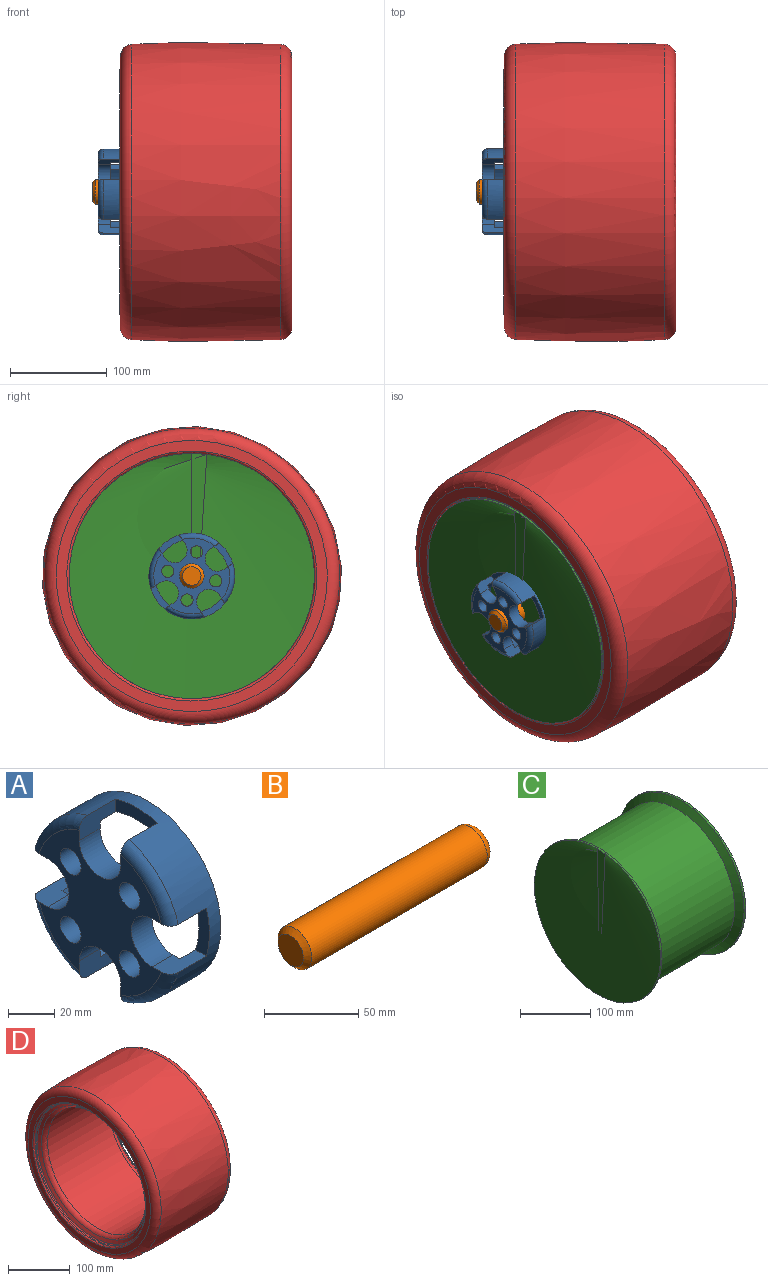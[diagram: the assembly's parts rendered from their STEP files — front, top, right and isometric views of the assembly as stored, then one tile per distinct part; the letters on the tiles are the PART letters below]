
ASSEMBLY  parts=4 mates=3
PART A: 29 faces, bbox 29.2x92.2x92.2 mm
  f0: cylinder r=38.1mm len=76.2mm, axis (1,0,0), area 2965.7mm2, adj f2,f8,f10,f11,f12,f14,f15,f16
  f1: plane 74.53x74.53mm, normal (-1,0,0), area 2645.6mm2, adj f3,f4,f5,f6,f9,f10,f11,f13
  f2: plane 71.84x71.84mm, normal (1,0,0), area 2468mm2, adj f0,f9,f10,f11,f13,f14,f15,f17
  f3: torus R=39.37mm, axis (-1,0,0), area 328.2mm2, adj f1,f7,f19,f23
  f4: torus R=39.37mm, axis (-1,0,0), area 328.2mm2, adj f1,f7,f14,f18
  f5: torus R=39.37mm, axis (-1,0,0), area 328.2mm2, adj f1,f7,f11,f15
  f6: torus R=39.37mm, axis (-1,0,0), area 328.2mm2, adj f1,f7,f10,f22
  f7: cylinder r=44.45mm len=88.9mm, axis (1,0,0), area 4972.7mm2, adj f3,f4,f5,f6,f8,f10,f11,f12
  f8: plane 88.9x88.9mm, normal (1,0,0), area 1646.8mm2, adj f0,f7
  f9: cylinder r=12.7mm len=25.4mm, axis (-1,0,0), area 506.7mm2, adj f1,f2,f10,f11
  f10: plane 22.23x10.85mm, normal (0,0,-1), area 195.6mm2, adj f0,f1,f2,f6,f7,f9,f12
  f11: plane 22.23x10.85mm, normal (0,0,1), area 195.6mm2, adj f0,f1,f2,f5,f7,f9,f12
  f12: plane 25.4x8.53mm, normal (-1,0,0), area 164mm2, adj f0,f7,f10,f11
  f13: cylinder r=12.7mm len=25.4mm, axis (-1,0,0), area 506.7mm2, adj f1,f2,f14,f15
  f14: plane 22.23x10.85mm, normal (0,1,0), area 195.6mm2, adj f0,f1,f2,f4,f7,f13,f16
  f15: plane 22.23x10.85mm, normal (0,-1,0), area 195.6mm2, adj f0,f1,f2,f5,f7,f13,f16
  f16: plane 25.4x8.53mm, normal (-1,0,0), area 164mm2, adj f0,f7,f14,f15
  f17: cylinder r=12.7mm len=25.4mm, axis (-1,0,0), area 506.7mm2, adj f1,f2,f18,f19
  f18: plane 22.23x10.85mm, normal (0,0,1), area 195.6mm2, adj f0,f1,f2,f4,f7,f17,f20
  f19: plane 22.23x10.85mm, normal (0,0,-1), area 195.6mm2, adj f0,f1,f2,f3,f7,f17,f20
  f20: plane 25.4x8.53mm, normal (-1,0,0), area 164mm2, adj f0,f7,f18,f19
  f21: cylinder r=12.7mm len=25.4mm, axis (-1,0,0), area 506.7mm2, adj f1,f2,f22,f23
  f22: plane 22.23x10.85mm, normal (0,-1,0), area 195.6mm2, adj f0,f1,f2,f6,f7,f21,f24
  f23: plane 22.23x10.85mm, normal (0,1,0), area 195.6mm2, adj f0,f1,f2,f3,f7,f21,f24
  f24: plane 25.4x8.53mm, normal (-1,0,0), area 164mm2, adj f0,f7,f22,f23
  f25: cylinder r=6.35mm len=12.7mm, axis (-1,0,0), area 506.7mm2, adj f1,f2
  f26: cylinder r=6.35mm len=12.7mm, axis (-1,0,0), area 506.7mm2, adj f1,f2
  f27: cylinder r=6.35mm len=12.7mm, axis (-1,0,0), area 506.7mm2, adj f1,f2
  f28: cylinder r=6.35mm len=12.7mm, axis (-1,0,0), area 506.7mm2, adj f1,f2
PART B: 5 faces, bbox 139.7x27.5x27.5 mm
  f0: cylinder r=12.7mm len=131.45mm, axis (1,0,0), area 10488.8mm2, adj f3,f4
  f1: plane 19.05x19.05mm, normal (-1,0,0), area 285mm2, adj f4
  f2: plane 15.24x15.24mm, normal (1,0,0), area 182.4mm2, adj f3
  f3: torus R=7.62mm, axis (1,0,0), area 544.2mm2, adj f0,f2
  f4: cone r=12.7mm half-angle=45deg, axis (1,0,0), area 313.5mm2, adj f0,f1
PART C: 238 faces, bbox 171.5x281.6x281.6 mm
  f0: cone r=44.45mm half-angle=87.1deg, axis (1,0,0), area 887.3mm2, adj f35,f36,f66,f72,f80,f83,f98,f101
  f1: cone r=44.45mm half-angle=87.1deg, axis (1,0,0), area 649.3mm2, adj f35,f36,f73,f81,f99,f145,f146
  f2: cone r=44.45mm half-angle=87.1deg, axis (1,0,0), area 887.3mm2, adj f35,f36,f62,f65,f82,f85,f100,f103
  f3: cone r=44.45mm half-angle=87.1deg, axis (1,0,0), area 887.3mm2, adj f35,f36,f43,f61,f84,f87,f102,f105
  f4: cone r=44.45mm half-angle=87.1deg, axis (1,0,0), area 887.3mm2, adj f35,f36,f54,f57,f76,f79,f92,f95
  f5: cone r=44.45mm half-angle=87.1deg, axis (1,0,0), area 649.3mm2, adj f35,f36,f53,f78,f94,f162,f165
  f6: cone r=44.45mm half-angle=87.1deg, axis (1,0,0), area 649.3mm2, adj f35,f36,f49,f74,f88,f183,f186
  f7: cone r=44.45mm half-angle=87.1deg, axis (1,0,0), area 649.3mm2, adj f35,f36,f58,f77,f93,f166,f168
  f8: cone r=44.45mm half-angle=87.1deg, axis (-1,0,0), area 442.3mm2, adj f38,f39,f127,f129,f130,f131
  f9: cone r=44.45mm half-angle=87.1deg, axis (-1,0,0), area 442.3mm2, adj f38,f39,f139,f141,f142,f143
  f10: cone r=44.45mm half-angle=87.1deg, axis (-1,0,0), area 442.3mm2, adj f38,f39,f115,f117,f118,f119
  f11: cone r=44.45mm half-angle=87.1deg, axis (-1,0,0), area 442.3mm2, adj f38,f39,f106,f107,f206,f208
  f12: cone r=44.45mm half-angle=87.1deg, axis (-1,0,0), area 442.3mm2, adj f38,f39,f214,f216,f231,f233
  f13: cone r=44.45mm half-angle=87.1deg, axis (-1,0,0), area 442.3mm2, adj f38,f39,f159,f163,f224,f225
  f14: cone r=44.45mm half-angle=87.1deg, axis (-1,0,0), area 442.3mm2, adj f38,f39,f187,f189,f190,f191
  f15: cone r=44.45mm half-angle=87.1deg, axis (-1,0,0), area 442.3mm2, adj f38,f39,f169,f172,f232,f234
  f16: cone r=107.95mm half-angle=71.6deg, axis (-1,0,0), area 10024.8mm2, adj f32,f33
  f17: cylinder r=107.95mm len=215.9mm, axis (-1,0,0), area 5780mm2, adj f33,f35
  f18: cone r=44.45mm half-angle=87.1deg, axis (1,0,0), area 887.3mm2, adj f35,f36,f42,f50,f75,f86,f89,f104
  f19: cylinder r=44.45mm len=88.9mm, axis (-1,0,0), area 2789.9mm2, adj f20,f36
  f20: plane 88.9x88.9mm, normal (-1,0,0), area 1646.8mm2, adj f19,f21
  f21: cylinder r=38.1mm len=82.55mm, axis (-1,0,0), area 19761.6mm2, adj f20,f22
  f22: plane 76.2x76.2mm, normal (-1,0,0), area 4560.4mm2, adj f21
  f23: plane 69.85x69.85mm, normal (1,0,0), area 3832mm2, adj f37
  f24: cylinder r=44.45mm len=88.9mm, axis (-1,0,0), area 10770.5mm2, adj f37,f38
  f25: cone r=44.45mm half-angle=87.1deg, axis (-1,0,0), area 442.3mm2, adj f38,f39,f199,f201,f205,f207
  f26: cylinder r=107.95mm len=215.9mm, axis (-1,0,0), area 74692.2mm2, adj f34,f39
  f27: cone r=107.95mm half-angle=71.6deg, axis (1,0,0), area 10024.8mm2, adj f28,f34
  f28: cylinder r=127mm len=254mm, axis (-1,0,0), area 2533.5mm2, adj f27,f29
  f29: cone r=114.3mm half-angle=63.4deg, axis (1,0,0), area 10763.8mm2, adj f28,f30
  f30: cylinder r=114.3mm len=228.6mm, axis (-1,0,0), area 109448.8mm2, adj f29,f31
  f31: cone r=114.3mm half-angle=63.4deg, axis (-1,0,0), area 10763.8mm2, adj f30,f32
  f32: cylinder r=127mm len=254mm, axis (-1,0,0), area 2533.5mm2, adj f16,f31
  f33: torus R=117.47mm, axis (1,0,0), area 8240.7mm2, adj f16,f17
  f34: torus R=117.47mm, axis (1,0,0), area 8240.7mm2, adj f26,f27
  f35: torus R=98.42mm, axis (-1,0,0), area 9680.5mm2, adj f0,f1,f2,f3,f4,f5,f6,f7
  f36: torus R=53.98mm, axis (-1,0,0), area 3935.7mm2, adj f0,f1,f2,f3,f4,f5,f6,f7
  f37: torus R=34.92mm, axis (-1,0,0), area 3853.3mm2, adj f23,f24
  f38: torus R=53.98mm, axis (-1,0,0), area 3464.9mm2, adj f8,f9,f10,f11,f12,f13,f14,f15
  f39: torus R=98.42mm, axis (-1,0,0), area 8487.7mm2, adj f8,f9,f10,f11,f12,f13,f14,f15
  f40: cylinder r=50.8mm len=9.79mm, axis (1,0,0), area 46.1mm2, adj f36,f104,f105,f213
  f41: cylinder r=98.42mm len=28.43mm, axis (1,0,0), area 93.3mm2, adj f35,f86,f87,f202
  f42: plane 32.91x6.73mm, normal (0,0.98,0.19), area 170.7mm2, adj f18,f86,f104,f207,f209
  f43: plane 25.3x22mm, normal (0,-0.75,0.66), area 170.7mm2, adj f3,f87,f105,f208,f210
  f44: cylinder r=50.8mm len=6.72mm, axis (1,0,0), area 31.7mm2, adj f90,f91,f174,f181
  f45: plane 17.38x1.73mm, normal (0,-0.02,1), area 14.8mm2, adj f90,f166,f167,f169,f173
  f46: plane 13.51x10.94mm, normal (0,-0.78,-0.63), area 14.8mm2, adj f91,f182,f186,f188,f189
  f47: cylinder r=50.8mm len=9.79mm, axis (1,0,0), area 46.1mm2, adj f36,f88,f89,f196
  f48: cylinder r=98.42mm len=26.67mm, axis (1,0,0), area 93.3mm2, adj f35,f74,f75,f195
  f49: plane 26.05x21.1mm, normal (0,0.63,0.78), area 170.7mm2, adj f6,f74,f88,f190,f192
  f50: plane 33.52x6.73mm, normal (0,-1,0.02), area 170.7mm2, adj f18,f75,f89,f200,f201
  f51: cylinder r=50.8mm len=9.79mm, axis (1,0,0), area 46.1mm2, adj f36,f94,f95,f219
  f52: cylinder r=98.42mm len=24.11mm, axis (1,0,0), area 93.3mm2, adj f35,f78,f79,f220
  f53: plane 33.11x6.73mm, normal (0,-0.99,0.16), area 170.7mm2, adj f5,f78,f94,f223,f225
  f54: plane 29.32x16.25mm, normal (0,0.48,-0.87), area 170.7mm2, adj f4,f79,f95,f214,f215
  f55: cylinder r=50.8mm len=9.79mm, axis (1,0,0), area 46.1mm2, adj f36,f92,f93,f226
  f56: cylinder r=98.42mm len=28.43mm, axis (1,0,0), area 93.3mm2, adj f35,f76,f77,f237
  f57: plane 25.3x22mm, normal (0,-0.66,0.75), area 170.7mm2, adj f4,f76,f92,f229,f231
  f58: plane 32.91x6.73mm, normal (0,-0.19,-0.98), area 170.7mm2, adj f7,f77,f93,f230,f232
  f59: cylinder r=50.8mm len=9.79mm, axis (1,0,0), area 46.1mm2, adj f36,f102,f103,f112
  f60: cylinder r=98.42mm len=24.11mm, axis (1,0,0), area 93.3mm2, adj f35,f84,f85,f111
  f61: plane 29.32x16.25mm, normal (0,0.87,-0.48), area 170.7mm2, adj f3,f84,f102,f106,f108
  f62: plane 33.11x6.73mm, normal (0,-0.16,0.99), area 170.7mm2, adj f2,f85,f103,f116,f117
  f63: cylinder r=50.8mm len=9.79mm, axis (1,0,0), area 46.1mm2, adj f36,f100,f101,f124
  f64: cylinder r=98.42mm len=29.32mm, axis (1,0,0), area 93.3mm2, adj f35,f82,f83,f123
  f65: plane 31.3x12.01mm, normal (0,0.36,-0.93), area 170.7mm2, adj f2,f82,f100,f118,f120
  f66: plane 28.74x17.27mm, normal (0,0.52,0.86), area 170.7mm2, adj f0,f83,f101,f128,f129
  f67: cylinder r=50.8mm len=6.72mm, axis (1,0,0), area 31.7mm2, adj f96,f97,f152,f157
  f68: plane 14.9x8.95mm, normal (0,-0.86,-0.52), area 14.8mm2, adj f96,f142,f144,f145,f149
  f69: plane 16.23x6.23mm, normal (0,0.93,-0.36), area 14.8mm2, adj f97,f160,f163,f164,f165
  f70: cylinder r=50.8mm len=9.79mm, axis (1,0,0), area 46.1mm2, adj f36,f98,f99,f136
  f71: cylinder r=98.42mm len=20.81mm, axis (1,0,0), area 93.3mm2, adj f35,f80,f81,f135
  f72: plane 31.7x10.92mm, normal (0,-0.33,-0.95), area 170.7mm2, adj f0,f80,f98,f130,f132
  f73: plane 31.7x10.92mm, normal (0,0.95,0.33), area 170.7mm2, adj f1,f81,f99,f140,f141
  f74: cylinder r=9.53mm len=15.34mm, axis (1,0,0), area 51.6mm2, adj f6,f35,f48,f49,f191,f193
  f75: cylinder r=9.53mm len=12.21mm, axis (1,0,0), area 51.6mm2, adj f18,f35,f48,f50,f197,f199
  f76: cylinder r=9.53mm len=14.98mm, axis (1,0,0), area 51.6mm2, adj f4,f35,f56,f57,f233,f235
  f77: cylinder r=9.53mm len=11.34mm, axis (1,0,0), area 51.6mm2, adj f7,f35,f56,f58,f234,f236
  f78: cylinder r=9.53mm len=13.64mm, axis (1,0,0), area 51.6mm2, adj f5,f35,f52,f53,f222,f224
  f79: cylinder r=9.53mm len=15.23mm, axis (1,0,0), area 51.6mm2, adj f4,f35,f52,f54,f216,f218
  f80: cylinder r=9.53mm len=14.66mm, axis (1,0,0), area 51.6mm2, adj f0,f35,f71,f72,f131,f133
  f81: cylinder r=9.53mm len=14.66mm, axis (1,0,0), area 51.6mm2, adj f1,f35,f71,f73,f137,f139
  f82: cylinder r=9.53mm len=12.92mm, axis (1,0,0), area 51.6mm2, adj f2,f35,f64,f65,f119,f121
  f83: cylinder r=9.53mm len=14.16mm, axis (1,0,0), area 51.6mm2, adj f0,f35,f64,f66,f125,f127
  f84: cylinder r=9.53mm len=15.23mm, axis (1,0,0), area 51.6mm2, adj f3,f35,f60,f61,f107,f109
  f85: cylinder r=9.53mm len=13.64mm, axis (1,0,0), area 51.6mm2, adj f2,f35,f60,f62,f113,f115
  f86: cylinder r=9.53mm len=11.34mm, axis (1,0,0), area 51.6mm2, adj f18,f35,f41,f42,f203,f205
  f87: cylinder r=9.53mm len=14.98mm, axis (1,0,0), area 51.6mm2, adj f3,f35,f41,f43,f204,f206
  f88: cylinder r=5.08mm len=9.79mm, axis (1,0,0), area 48.7mm2, adj f6,f36,f47,f49,f194
  f89: cylinder r=5.08mm len=9.79mm, axis (1,0,0), area 48.7mm2, adj f18,f36,f47,f50,f198
  f90: cylinder r=5.08mm len=6.72mm, axis (1,0,0), area 25mm2, adj f44,f45,f170,f177
  f91: cylinder r=5.08mm len=6.72mm, axis (1,0,0), area 25mm2, adj f44,f46,f178,f185
  f92: cylinder r=5.08mm len=9.79mm, axis (1,0,0), area 48.7mm2, adj f4,f36,f55,f57,f227
  f93: cylinder r=5.08mm len=9.79mm, axis (1,0,0), area 48.7mm2, adj f7,f36,f55,f58,f228
  f94: cylinder r=5.08mm len=9.79mm, axis (1,0,0), area 48.7mm2, adj f5,f36,f51,f53,f221
  f95: cylinder r=5.08mm len=9.79mm, axis (1,0,0), area 48.7mm2, adj f4,f36,f51,f54,f217
  f96: cylinder r=5.08mm len=6.72mm, axis (1,0,0), area 25mm2, adj f67,f68,f148,f153
  f97: cylinder r=5.08mm len=6.72mm, axis (1,0,0), area 25mm2, adj f67,f69,f156,f161
  f98: cylinder r=5.08mm len=9.79mm, axis (1,0,0), area 48.7mm2, adj f0,f36,f70,f72,f134
  f99: cylinder r=5.08mm len=9.79mm, axis (1,0,0), area 48.7mm2, adj f1,f36,f70,f73,f138
  f100: cylinder r=5.08mm len=9.79mm, axis (1,0,0), area 48.7mm2, adj f2,f36,f63,f65,f122
  f101: cylinder r=5.08mm len=9.79mm, axis (1,0,0), area 48.7mm2, adj f0,f36,f63,f66,f126
  f102: cylinder r=5.08mm len=9.79mm, axis (1,0,0), area 48.7mm2, adj f3,f36,f59,f61,f110
  f103: cylinder r=5.08mm len=9.79mm, axis (1,0,0), area 48.7mm2, adj f2,f36,f59,f62,f114
  f104: cylinder r=5.08mm len=9.79mm, axis (1,0,0), area 48.7mm2, adj f18,f36,f40,f42,f211
  f105: cylinder r=5.08mm len=9.79mm, axis (1,0,0), area 48.7mm2, adj f3,f36,f40,f43,f212
  f106: bspline ~55.61x33.72mm, area 261.8mm2, adj f11,f61,f107,f108
  f107: bspline ~12.89x11.12mm, area 81.1mm2, adj f11,f84,f106,f109
  f108: bspline ~5.27x5.21mm, area 3.6mm2, adj f38,f61,f106,f110
  f109: bspline ~14.81x8.92mm, area 74.2mm2, adj f39,f84,f107,f111
  f110: bspline ~12.45x6.75mm, area 48.2mm2, adj f38,f102,f108,f112
  f111: torus R=103.5mm, axis (1,0,0), area 184.6mm2, adj f39,f60,f109,f113
  f112: torus R=45.72mm, axis (1,0,0), area 22.9mm2, adj f38,f59,f110,f114
  f113: bspline ~16.25x6.27mm, area 74.2mm2, adj f39,f85,f111,f115
  f114: bspline ~9.93x8.48mm, area 48.2mm2, adj f38,f103,f112,f116
  f115: bspline ~13.19x10.84mm, area 81.1mm2, adj f10,f85,f113,f117
  f116: bspline ~5.21x5.15mm, area 3.6mm2, adj f38,f62,f114,f117
  f117: bspline ~92.64x19.47mm, area 261.8mm2, adj f10,f62,f115,f116
  f118: bspline ~98.27x41.85mm, area 261.8mm2, adj f10,f65,f119,f120
  f119: bspline ~15.37x7.09mm, area 81.1mm2, adj f10,f82,f118,f121
  f120: bspline ~5.45x5.14mm, area 3.6mm2, adj f38,f65,f118,f122
  f121: bspline ~13.65x9.62mm, area 74.2mm2, adj f39,f82,f119,f123
  f122: bspline ~11.84x6.75mm, area 48.2mm2, adj f38,f100,f120,f124
  f123: torus R=103.5mm, axis (1,0,0), area 184.6mm2, adj f39,f64,f121,f125
  f124: torus R=45.72mm, axis (1,0,0), area 22.9mm2, adj f38,f63,f122,f126
  f125: bspline ~13.69x11.18mm, area 74.2mm2, adj f39,f83,f123,f127
  f126: bspline ~12.33x6.75mm, area 48.2mm2, adj f38,f101,f124,f128
  f127: bspline ~15.35x7.14mm, area 81.1mm2, adj f8,f83,f125,f129
  f128: bspline ~5.79x5.21mm, area 3.6mm2, adj f38,f66,f126,f129
  f129: bspline ~82.09x52.23mm, area 261.8mm2, adj f8,f66,f127,f128
  f130: bspline ~99.59x38.38mm, area 261.8mm2, adj f8,f72,f131,f132
  f131: bspline ~12.34x12.05mm, area 81.1mm2, adj f8,f80,f130,f133
  f132: bspline ~5.17x5.14mm, area 3.6mm2, adj f38,f72,f130,f134
  f133: bspline ~15.77x7.14mm, area 74.2mm2, adj f39,f80,f131,f135
  f134: bspline ~11.64x7.25mm, area 48.2mm2, adj f38,f98,f132,f136
  f135: torus R=103.5mm, axis (1,0,0), area 184.6mm2, adj f39,f71,f133,f137
  f136: torus R=45.72mm, axis (1,0,0), area 22.9mm2, adj f38,f70,f134,f138
  f137: bspline ~15.77x7.14mm, area 74.2mm2, adj f39,f81,f135,f139
  f138: bspline ~11.13x7.26mm, area 48.2mm2, adj f38,f99,f136,f140
  f139: bspline ~12.34x12.05mm, area 81.1mm2, adj f9,f81,f137,f141
  f140: bspline ~5.29x5.21mm, area 3.6mm2, adj f38,f73,f138,f141
  f141: bspline ~89.58x34.94mm, area 261.8mm2, adj f9,f73,f139,f140
  f142: bspline ~82.61x52.55mm, area 255.4mm2, adj f9,f68,f143,f144,f145
  f143: bspline ~14.22x7.14mm, area 71.7mm2, adj f9,f142,f146,f147
  f144: bspline ~5.35x5.14mm, area 3.6mm2, adj f38,f68,f142,f148
  f145: bspline ~83.92x53.33mm, area 255.4mm2, adj f1,f68,f142,f146,f149
  f146: bspline ~15.35x7.14mm, area 71.7mm2, adj f1,f143,f145,f150
  f147: bspline ~13.69x11.18mm, area 65.7mm2, adj f39,f143,f150,f151
  f148: bspline ~12.57x6.75mm, area 48.2mm2, adj f38,f96,f144,f152
  f149: bspline ~5.79x5.21mm, area 3.6mm2, adj f36,f68,f145,f153
  f150: bspline ~13.69x11.18mm, area 65.7mm2, adj f35,f146,f147,f154
  f151: torus R=103.5mm, axis (1,0,0), area 169.6mm2, adj f39,f147,f154,f155
  f152: torus R=45.72mm, axis (1,0,0), area 22.9mm2, adj f38,f67,f148,f156
  f153: bspline ~12.33x6.75mm, area 48.2mm2, adj f36,f96,f149,f157
  f154: torus R=103.5mm, axis (-1,0,0), area 169.6mm2, adj f35,f150,f151,f158
  f155: bspline ~13.65x9.62mm, area 65.7mm2, adj f39,f151,f158,f159
  f156: bspline ~11.69x6.75mm, area 48.2mm2, adj f38,f97,f152,f160
  f157: torus R=45.72mm, axis (-1,0,0), area 22.9mm2, adj f36,f67,f153,f161
  f158: bspline ~13.65x9.62mm, area 65.7mm2, adj f35,f154,f155,f162
  f159: bspline ~15.37x7.09mm, area 71.8mm2, adj f13,f155,f162,f163
  f160: bspline ~5.75x5.21mm, area 3.6mm2, adj f38,f69,f156,f163
  f161: bspline ~11.84x6.75mm, area 48.2mm2, adj f36,f97,f157,f164
  f162: bspline ~15.37x7.09mm, area 71.8mm2, adj f5,f158,f159,f165
  f163: bspline ~88.39x38.05mm, area 255.4mm2, adj f13,f69,f159,f160,f165
  f164: bspline ~5.45x5.14mm, area 3.6mm2, adj f36,f69,f161,f165
  f165: bspline ~88.96x38.27mm, area 255.4mm2, adj f5,f69,f162,f163,f164
  f166: bspline ~95.12x9.77mm, area 255.4mm2, adj f7,f45,f167,f168,f169
  f167: bspline ~5.21x5.16mm, area 3.6mm2, adj f36,f45,f166,f170
  f168: bspline ~14.04x9.43mm, area 71.7mm2, adj f7,f166,f171,f172
  f169: bspline ~103.57x10.18mm, area 255.4mm2, adj f15,f45,f166,f172,f173
  f170: bspline ~9.59x8.43mm, area 48.2mm2, adj f36,f90,f167,f174
  f171: bspline ~16.23x7.04mm, area 65.7mm2, adj f35,f168,f175,f176
  f172: bspline ~13.31x8.78mm, area 71.7mm2, adj f15,f168,f169,f176
  f173: bspline ~5.21x5.16mm, area 3.6mm2, adj f38,f45,f169,f177
  f174: torus R=45.72mm, axis (-1,0,0), area 22.9mm2, adj f36,f44,f170,f178
  f175: torus R=103.5mm, axis (-1,0,0), area 169.6mm2, adj f35,f171,f179,f180
  f176: bspline ~16.23x7.04mm, area 65.7mm2, adj f39,f171,f172,f180
  f177: bspline ~9.59x8.99mm, area 48.2mm2, adj f38,f90,f173,f181
  f178: bspline ~12.88x6.75mm, area 48.2mm2, adj f36,f91,f174,f182
  f179: bspline ~13.4x10.78mm, area 65.7mm2, adj f35,f175,f183,f184
  f180: torus R=103.5mm, axis (1,0,0), area 169.6mm2, adj f39,f175,f176,f184
  f181: torus R=45.72mm, axis (1,0,0), area 22.9mm2, adj f38,f44,f177,f185
  f182: bspline ~5.2x4.85mm, area 3.6mm2, adj f36,f46,f178,f186
  f183: bspline ~13.91x9.65mm, area 71.8mm2, adj f6,f179,f186,f187
  f184: bspline ~13.4x10.78mm, area 65.7mm2, adj f39,f179,f180,f187
  f185: bspline ~12.48x6.75mm, area 48.2mm2, adj f38,f91,f181,f188
  f186: bspline ~83.69x68.93mm, area 255.4mm2, adj f6,f46,f182,f183,f189
  f187: bspline ~13.91x9.65mm, area 71.8mm2, adj f14,f183,f184,f189
  f188: bspline ~5.2x4.85mm, area 3.6mm2, adj f38,f46,f185,f189
  f189: bspline ~75.46x62.27mm, area 255.4mm2, adj f14,f46,f186,f187,f188
  f190: bspline ~83.69x68.93mm, area 261.8mm2, adj f14,f49,f191,f192
  f191: bspline ~13.91x9.65mm, area 81.1mm2, adj f14,f74,f190,f193
  f192: bspline ~5.14x4.78mm, area 3.6mm2, adj f38,f49,f190,f194
  f193: bspline ~13.4x10.78mm, area 74.2mm2, adj f39,f74,f191,f195
  f194: bspline ~12.88x6.75mm, area 48.2mm2, adj f38,f88,f192,f196
  f195: torus R=103.5mm, axis (1,0,0), area 184.6mm2, adj f39,f48,f193,f197
  f196: torus R=45.72mm, axis (1,0,0), area 22.9mm2, adj f38,f47,f194,f198
  f197: bspline ~16.23x7.04mm, area 74.2mm2, adj f39,f75,f195,f199
  f198: bspline ~9.59x8.43mm, area 48.2mm2, adj f38,f89,f196,f200
  f199: bspline ~12.83x9.43mm, area 81.1mm2, adj f25,f75,f197,f201
  f200: bspline ~5.21x5.16mm, area 3.6mm2, adj f38,f50,f198,f201
  f201: bspline ~92.98x9.66mm, area 261.8mm2, adj f25,f50,f199,f200
  f202: torus R=103.5mm, axis (1,0,0), area 184.6mm2, adj f39,f41,f203,f204
  f203: bspline ~15.73x8.16mm, area 74.2mm2, adj f39,f86,f202,f205
  f204: bspline ~12.42x12.39mm, area 74.2mm2, adj f39,f87,f202,f206
  f205: bspline ~14.93x8.16mm, area 81.1mm2, adj f25,f86,f203,f207
  f206: bspline ~14.85x8.3mm, area 81.1mm2, adj f11,f87,f204,f208
  f207: bspline ~102.4x24.73mm, area 261.8mm2, adj f25,f42,f205,f209
  f208: bspline ~73.29x64.83mm, area 261.8mm2, adj f11,f43,f206,f210
  f209: bspline ~5.38x5.14mm, area 3.6mm2, adj f38,f42,f207,f211
  f210: bspline ~5.65x5.21mm, area 3.6mm2, adj f38,f43,f208,f212
  f211: bspline ~10.74x7.46mm, area 48.2mm2, adj f38,f104,f209,f213
  f212: bspline ~12.6x6.75mm, area 48.2mm2, adj f38,f105,f210,f213
  f213: torus R=45.72mm, axis (1,0,0), area 22.9mm2, adj f38,f40,f211,f212
  f214: bspline ~83.79x49.36mm, area 261.8mm2, adj f12,f54,f215,f216
  f215: bspline ~5.27x5.21mm, area 3.6mm2, adj f38,f54,f214,f217
  f216: bspline ~12.89x11.12mm, area 81.1mm2, adj f12,f79,f214,f218
  f217: bspline ~11.99x6.75mm, area 48.2mm2, adj f38,f95,f215,f219
  f218: bspline ~14.03x8.23mm, area 74.2mm2, adj f39,f79,f216,f220
  f219: torus R=45.72mm, axis (1,0,0), area 22.9mm2, adj f38,f51,f217,f221
  f220: torus R=103.5mm, axis (1,0,0), area 184.6mm2, adj f39,f52,f218,f222
  f221: bspline ~10.47x8.48mm, area 48.2mm2, adj f38,f94,f219,f223
  f222: bspline ~16.25x6.27mm, area 74.2mm2, adj f39,f78,f220,f224
  f223: bspline ~5.14x5.13mm, area 3.6mm2, adj f38,f53,f221,f225
  f224: bspline ~13.19x10.84mm, area 81.1mm2, adj f13,f78,f222,f225
  f225: bspline ~103.11x21.11mm, area 261.8mm2, adj f13,f53,f223,f224
  f226: torus R=45.72mm, axis (1,0,0), area 22.9mm2, adj f38,f55,f227,f228
  f227: bspline ~12.92x6.75mm, area 48.2mm2, adj f38,f92,f226,f229
  f228: bspline ~10.7x7.12mm, area 48.2mm2, adj f38,f93,f226,f230
  f229: bspline ~5.65x5.21mm, area 3.6mm2, adj f38,f57,f227,f231
  f230: bspline ~5.54x5.21mm, area 3.6mm2, adj f38,f58,f228,f232
  f231: bspline ~81.28x71.78mm, area 261.8mm2, adj f12,f57,f229,f233
  f232: bspline ~92x22.71mm, area 261.8mm2, adj f15,f58,f230,f234
  f233: bspline ~14.85x8.31mm, area 81.1mm2, adj f12,f76,f231,f235
  f234: bspline ~14.93x8.16mm, area 81.1mm2, adj f15,f77,f232,f236
  f235: bspline ~12.42x12.39mm, area 74.2mm2, adj f39,f76,f233,f237
  f236: bspline ~15.73x8.16mm, area 74.2mm2, adj f39,f77,f234,f237
  f237: torus R=103.5mm, axis (1,0,0), area 184.6mm2, adj f39,f56,f235,f236
PART D: 16 faces, bbox 177.8x331.5x331.5 mm
  f0: cylinder r=127mm len=254mm, axis (-1,0,0), area 1787.6mm2, adj f8,f11
  f1: plane 280.86x280.86mm, normal (1,0,0), area 9238.1mm2, adj f8,f14
  f2: revolved ~310.46x310.46mm, area 298792.3mm2, adj f14,f15
  f3: plane 280.85x280.85mm, normal (-1,0,0), area 9232mm2, adj f9,f15
  f4: cylinder r=127mm len=254mm, axis (-1,0,0), area 1787.6mm2, adj f9,f10
  f5: cone r=114.3mm half-angle=63.4deg, axis (-1,0,0), area 5193mm2, adj f10,f12
  f6: cylinder r=114.3mm len=228.6mm, axis (-1,0,0), area 100993.4mm2, adj f12,f13
  f7: cone r=114.3mm half-angle=63.4deg, axis (1,0,0), area 5193mm2, adj f11,f13
  f8: torus R=129.54mm, axis (1,0,0), area 3206.9mm2, adj f0,f1
  f9: torus R=129.54mm, axis (1,0,0), area 3206.9mm2, adj f3,f4
  f10: torus R=124.46mm, axis (-1,0,0), area 2235.4mm2, adj f4,f5
  f11: torus R=124.46mm, axis (-1,0,0), area 2235.4mm2, adj f0,f7
  f12: torus R=123.83mm, axis (1,0,0), area 7694.8mm2, adj f5,f6
  f13: torus R=123.83mm, axis (1,0,0), area 7694.8mm2, adj f6,f7
  f14: torus R=140.43mm, axis (1,0,0), area 17943.3mm2, adj f1,f2
  f15: torus R=140.43mm, axis (1,0,0), area 17941.4mm2, adj f2,f3
PLACE A rot(axis=(1,0,0),56.3deg) t=(-80.11,-23.01,12.87)mm
PLACE B rot(axis=(-1,0,0),1deg) t=(-80.11,-23.01,12.87)mm
PLACE C t=(-80.11,-23.01,12.87)mm fixed
PLACE D rot(axis=(1,0,0),99.3deg) t=(-76.23,-23.01,12.87)mm
MATE revolute A.f0 <-> B.f0  axis (-1,0,0) through (-149.96,-23.01,12.87)mm
MATE revolute B.f0 <-> C.f0  axis (1,0,0) through (-16.61,-23.01,12.87)mm
MATE revolute D.f0 <-> C.f0  axis (1,0,0) through (-123.56,-23.01,12.87)mm
